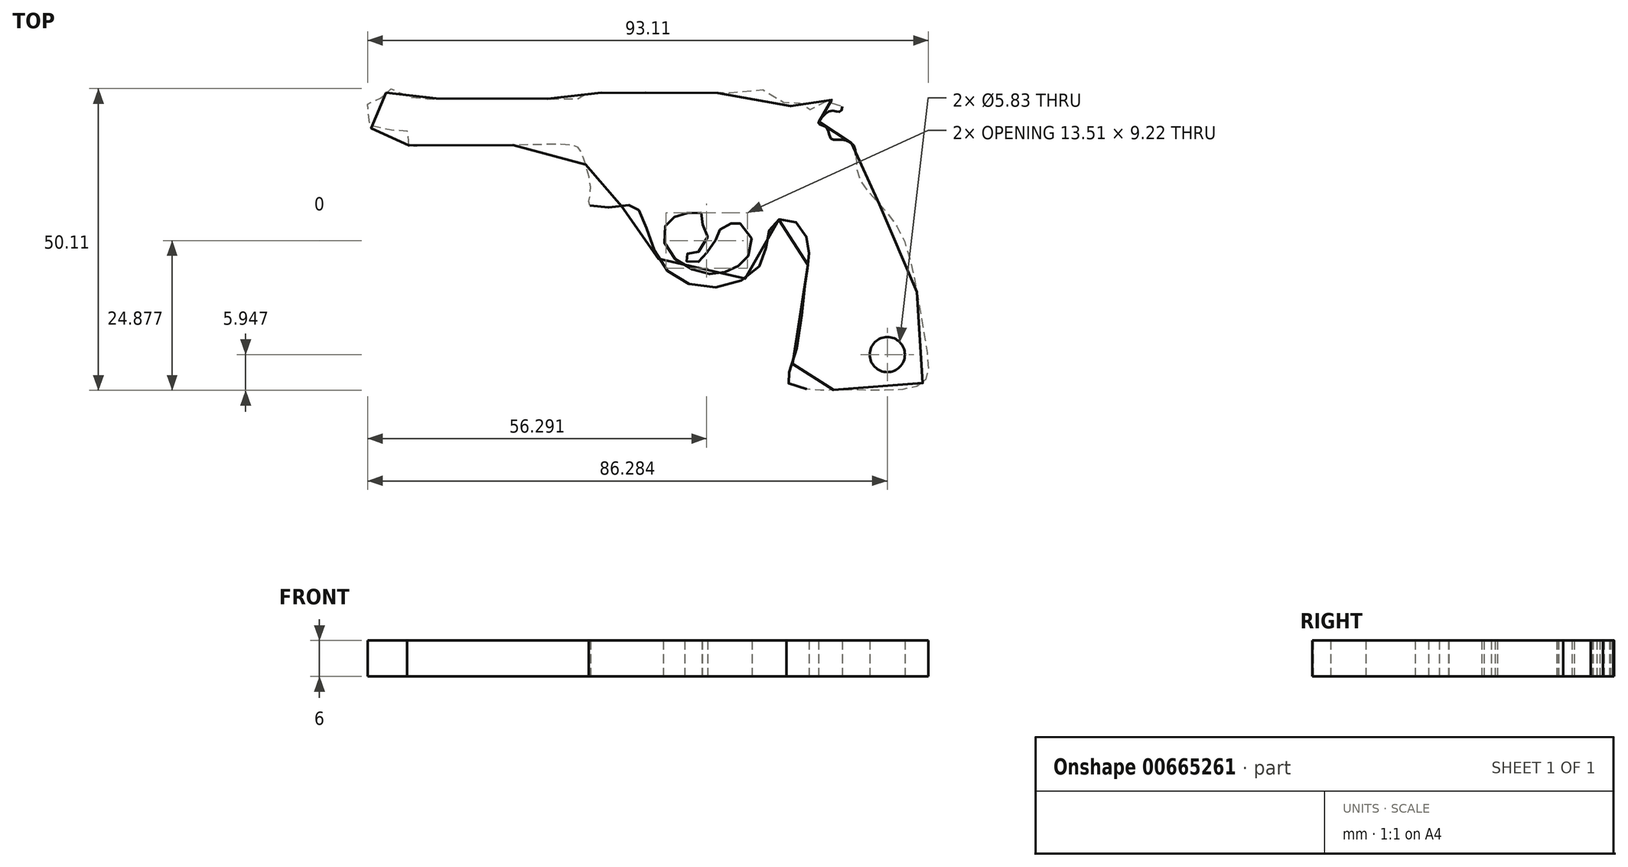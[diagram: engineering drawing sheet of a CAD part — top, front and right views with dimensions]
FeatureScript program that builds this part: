
annotation { "Feature Type Name" : "Feature", "Feature Type Description" : "" }
export const myFeature = defineFeature(function(context is Context, id is Id, definition is map)
    precondition{}
    {
        {
            var Q0;
            Q0=qCreatedBy(makeId("Top.planeOp"),FACE);
            var sketch = newSketch(context, id + "F0", { "sketchPlane" : qUnion([Q0])});
            skPoint(sketch, "E0.55.internal.snap0", {"position": v(-9.98, 27.45) * mm});
            skFitSpline(sketch, "E0", {"points": [v(-49.6, 18.03) * mm, v(-49.89, 18.5) * mm, v(-49.84, 20.66) * mm, v(-50.46, 20.8) * mm, v(-55.63, 20.7) * mm, v(-56.2, 22.62) * mm, v(-56.2, 25.6) * mm, v(-54.3, 25.88) * mm, v(-53.38, 26.74) * mm, v(-52.1, 27.45) * mm, v(-48.93, 25.83) * mm, v(-47.45, 25.73) * mm, v(-41.18, 25.78) * mm, v(-28.97, 25.78) * mm, v(-20.88, 25.78) * mm, v(-20.45, 25.93) * mm, v(-19.97, 26.74) * mm, v(-18.58, 26.84) * mm, v(-7.57, 26.88) * mm, v(4.4, 26.84) * mm, v(10.8, 26.88) * mm, v(13.52, 24.59) * mm, v(15.38, 25.09) * mm, v(16.1, 24.87) * mm, v(17.32, 23.94) * mm, v(19.54, 25.3) * mm, v(22.2, 25.09) * mm, v(22.05, 23.65) * mm, v(20.69, 23.8) * mm, v(18.9, 22.58) * mm, v(18.47, 21.57) * mm, v(19.68, 21.07) * mm, v(20.55, 19.14) * mm, v(22.2, 19) * mm, v(24.35, 17.84) * mm, v(24.85, 13.61) * mm, v(27.07, 9.88) * mm, v(31.66, 4.22) * mm, v(34.32, -3.96) * mm, v(36.23, -15.06) * mm, v(36.23, -20.84) * mm, v(31.9, -22.55) * mm, v(22.46, -22.55) * mm, v(17.49, -22.55) * mm, v(13.23, -21.25) * mm, v(14.04, -18.51) * mm, v(16.07, -6.14) * mm, v(16.68, -1.67) * mm, v(16.78, 1.47) * mm, v(14.85, 5.12) * mm, v(11.4, 5.53) * mm, v(9.88, 2.49) * mm, v(8.56, -2.08) * mm, v(1.56, -5.53) * mm, v(-6.65, -2.79) * mm, v(-9.98, 3.9) * mm, v(-11.93, 7.86) * mm, v(-13.96, 7.96) * mm, v(-19.54, 8.06) * mm, v(-19.43, 10.2) * mm, v(-20.85, 16.58) * mm, v(-21.97, 17.9) * mm, v(-30.39, 18.1) * mm, v(-45.2, 18) * mm, v(-49.6, 18.03) * mm]});
            skFitSpline(sketch, "E1", {"points": [v(-1.06, 6.84) * mm, v(-3.86, 6.7) * mm, v(-5.73, 6.04) * mm, v(-7.26, 4.04) * mm, v(-6.2, 0) * mm, v(-1.8, -2.83) * mm, v(1.8, -3.3) * mm, v(4.6, -2.23) * mm, v(6.54, -0.63) * mm, v(7.07, 3.3) * mm, v(4.34, 5.44) * mm, v(3.74, 4.84) * mm, v(1.74, 3.77) * mm, v(1.27, 1.97) * mm, v(-0.8, -0.5) * mm, v(-1.86, -1.5) * mm, v(-3.73, -0.96) * mm, v(-3.46, 0) * mm, v(-2.2, 0) * mm, v(0, 2.84) * mm, v(-0.86, 5.04) * mm, v(-1.06, 6.84) * mm]});
            skCircle(sketch, "E2", {"center": v(29.85, -16.7) * mm, "radius": 2.91 * mm});
            skSolve(sketch);
        }
        {
            var Q0;
            Q0 = qSketchRegion(id + "F0", true);
            extrude(context, id + "F1", {"entities" : qUnion([Q0]), "depth" : 6 * mm, "offsetDistance" : 25.4 * mm});
        }
        {
            var Q0;
            Q0=sQuery(id+"F0.wireOp",EDGE,"E2");
            extrude(context, id + "F2", {"bodyType" : ToolBodyType.SURFACE, "surfaceEntities" : qUnion([Q0]), "depth" : 5 * mm, "offsetDistance" : 25 * mm});
        }
    });
